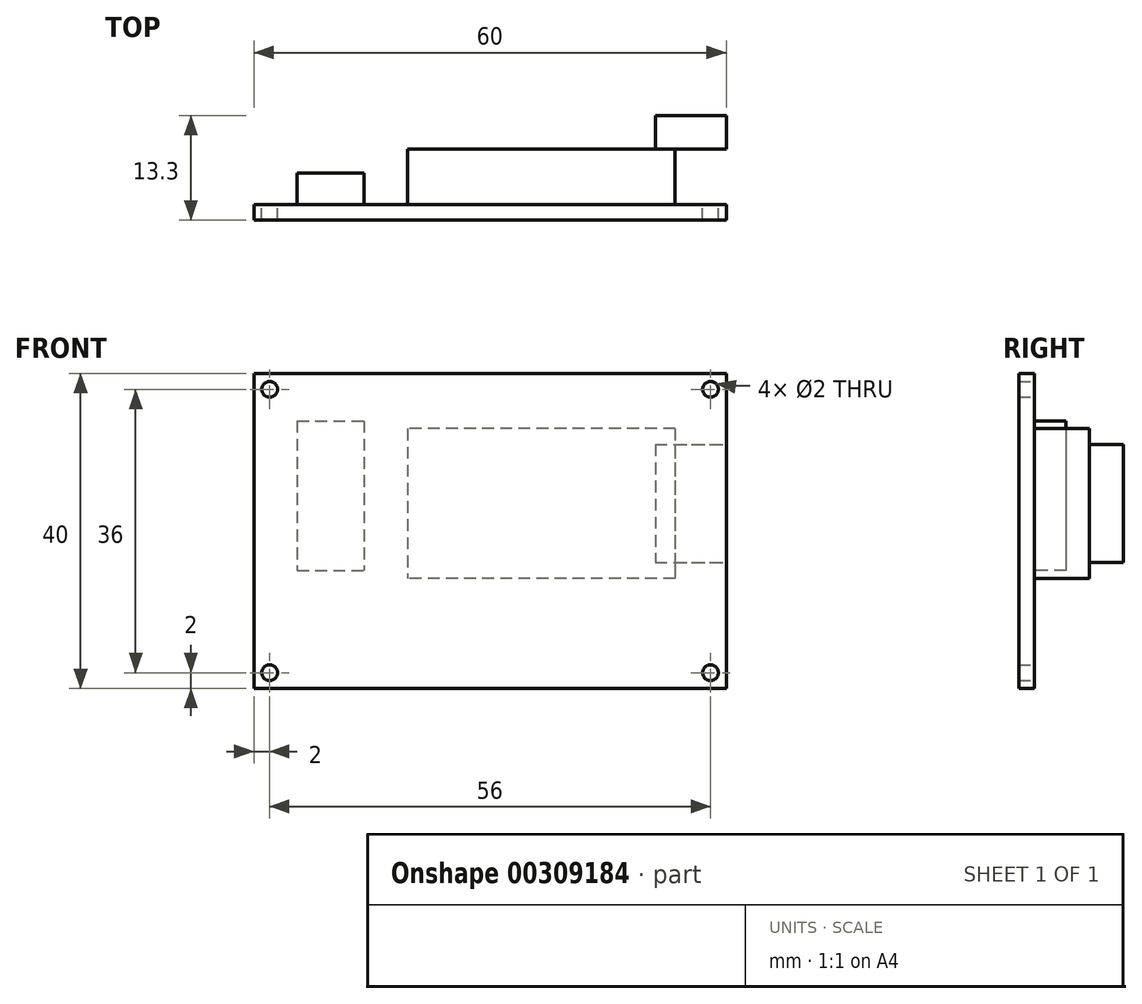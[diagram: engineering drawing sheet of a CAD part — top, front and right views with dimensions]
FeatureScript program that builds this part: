
annotation { "Feature Type Name" : "Feature", "Feature Type Description" : "" }
export const myFeature = defineFeature(function(context is Context, id is Id, definition is map)
    precondition{}
    {
        {
            var Q0;
            Q0=qCreatedBy(makeId("Front.planeOp"),FACE);
            var sketch = newSketch(context, id + "F0", { "sketchPlane" : qUnion([Q0])});
            skLineSegment(sketch, "E0.bottom", {"start": v(30, 20) * mm, "end": v(-30, 20) * mm});
            skLineSegment(sketch, "E0.top", {"start": v(30, -20) * mm, "end": v(-30, -20) * mm});
            skLineSegment(sketch, "E0.left", {"start": v(30, 20) * mm, "end": v(30, -20) * mm});
            skLineSegment(sketch, "E0.right", {"start": v(-30, 20) * mm, "end": v(-30, -20) * mm});
            skPoint(sketch, "E0.middle", {"position": v(0, 0) * mm});
            skCircle(sketch, "E1", {"center": v(-28, 18) * mm, "radius": 1 * mm});
            skCircle(sketch, "E2.MirrorC", {"center": v(28, 18) * mm, "radius": 1 * mm});
            skCircle(sketch, "E3.MirrorC", {"center": v(28, -18) * mm, "radius": 1 * mm});
            skCircle(sketch, "E4.MirrorC", {"center": v(-28, -18) * mm, "radius": 1 * mm});
            skSolve(sketch);
        }
        {
            var Q0;
            Q0=makeQuery(id+"F0.imprint","IMPRINT",FACE,{"disambiguationData":[TD([[makeQuery(id+"F0.imprint","IMPRINT",EDGE,{"derivedFrom":sQuery(id+"F0.wireOp",EDGE,"E0.bottom")}),1.0]])]});
            extrude(context, id + "F1", {"entities" : qUnion([Q0]), "depth" : 2 * mm});
        }
        {
            var Q0;
            Q0=makeQuery(id+"F1.opExtrude","CAP_FACE",FACE,{"disambiguationData":[OSD([sQuery(id+"F0.wireOp",EDGE,"E0.bottom"),sQuery(id+"F0.wireOp",EDGE,"E0.top"),sQuery(id+"F0.wireOp",EDGE,"E0.left"),sQuery(id+"F0.wireOp",EDGE,"E0.right"),sQuery(id+"F0.wireOp",EDGE,"E1"),sQuery(id+"F0.wireOp",EDGE,"E2.MirrorC"),sQuery(id+"F0.wireOp",EDGE,"E3.MirrorC"),sQuery(id+"F0.wireOp",EDGE,"E4.MirrorC")])],"isStart":true});
            var sketch = newSketch(context, id + "F2", { "sketchPlane" : qUnion([Q0])});
            skLineSegment(sketch, "E5.bottom", {"start": v(24.5, 14) * mm, "end": v(16, 14) * mm});
            skLineSegment(sketch, "E5.top", {"start": v(24.5, -5) * mm, "end": v(16, -5) * mm});
            skLineSegment(sketch, "E5.left", {"start": v(24.5, 14) * mm, "end": v(24.5, -5) * mm});
            skLineSegment(sketch, "E5.right", {"start": v(16, 14) * mm, "end": v(16, -5) * mm});
            skSolve(sketch);
        }
        {
            var Q0;
            Q0 = qSketchRegion(id + "F2", true);
            extrude(context, id + "F3", {"entities" : qUnion([Q0]), "operationType" : NewBodyOperationType.ADD, "depth" : 4 * mm});
        }
        {
            var Q0;
            Q0=makeQuery(id+"F1.opExtrude","CAP_FACE",FACE,{"disambiguationData":[OSD([sQuery(id+"F0.wireOp",EDGE,"E0.bottom"),sQuery(id+"F0.wireOp",EDGE,"E0.top"),sQuery(id+"F0.wireOp",EDGE,"E0.left"),sQuery(id+"F0.wireOp",EDGE,"E0.right"),sQuery(id+"F0.wireOp",EDGE,"E1"),sQuery(id+"F0.wireOp",EDGE,"E2.MirrorC"),sQuery(id+"F0.wireOp",EDGE,"E3.MirrorC"),sQuery(id+"F0.wireOp",EDGE,"E4.MirrorC")])],"isStart":true});
            var sketch = newSketch(context, id + "F4", { "sketchPlane" : qUnion([Q0])});
            skLineSegment(sketch, "E6.bottom", {"start": v(-23.5, 13) * mm, "end": v(10.5, 13) * mm});
            skLineSegment(sketch, "E6.top", {"start": v(-23.5, -6) * mm, "end": v(10.5, -6) * mm});
            skLineSegment(sketch, "E6.left", {"start": v(-23.5, 13) * mm, "end": v(-23.5, -6) * mm});
            skLineSegment(sketch, "E6.right", {"start": v(10.5, 13) * mm, "end": v(10.5, -6) * mm});
            skSolve(sketch);
        }
        {
            var Q0;
            Q0=makeQuery(id+"F4.imprint","IMPRINT",FACE,{"disambiguationData":[TD([[makeQuery(id+"F4.imprint","IMPRINT",EDGE,{"derivedFrom":sQuery(id+"F4.wireOp",EDGE,"E6.bottom")}),-1.0]])]});
            extrude(context, id + "F5", {"entities" : qUnion([Q0]), "operationType" : NewBodyOperationType.ADD, "depth" : 7 * mm});
        }
        {
            var Q0;
            Q0=makeQuery(id+"F5.opExtrude","CAP_FACE",FACE,{"disambiguationData":[OSD([sQuery(id+"F4.wireOp",EDGE,"E6.bottom"),sQuery(id+"F4.wireOp",EDGE,"E6.top"),sQuery(id+"F4.wireOp",EDGE,"E6.left"),sQuery(id+"F4.wireOp",EDGE,"E6.right")])],"isStart":false});
            var sketch = newSketch(context, id + "F6", { "sketchPlane" : qUnion([Q0])});
            skLineSegment(sketch, "E7.bottom", {"start": v(-21, 11) * mm, "end": v(-30, 11) * mm});
            skLineSegment(sketch, "E7.top", {"start": v(-21, -4) * mm, "end": v(-30, -4) * mm});
            skLineSegment(sketch, "E7.left", {"start": v(-21, 11) * mm, "end": v(-21, -4) * mm});
            skLineSegment(sketch, "E7.right", {"start": v(-30, 11) * mm, "end": v(-30, -4) * mm});
            skLineSegment(sketch, "E8", {"start": v(-23.5, 3.5) * mm, "end": v(10.5, 3.5) * mm, "construction": true});
            skLineSegment(sketch, "E9", {"start": v(-21, 3.5) * mm, "end": v(-30, 3.5) * mm, "construction": true});
            skSolve(sketch);
        }
        {
            var Q0;
            {var subQ0=sQuery(id+"F6.wireOp",EDGE,"E7.left");Q0=makeQuery(id+"F6.imprint","IMPRINT",FACE,{"disambiguationData":[TD([[makeQuery(id+"F6.imprint","IMPRINT",EDGE,{"derivedFrom":subQ0}),-1.0]])]});}
            var Q1;
            {var subQ0=sQuery(id+"F6.wireOp",EDGE,"E7.right");Q1=makeQuery(id+"F6.imprint","IMPRINT",FACE,{"disambiguationData":[TD([[makeQuery(id+"F6.imprint","IMPRINT",EDGE,{"derivedFrom":subQ0}),1.0]])]});}
            extrude(context, id + "F7", {"entities" : qUnion([Q0, Q1]), "operationType" : NewBodyOperationType.ADD, "depth" : 4.3 * mm});
        }
    });
